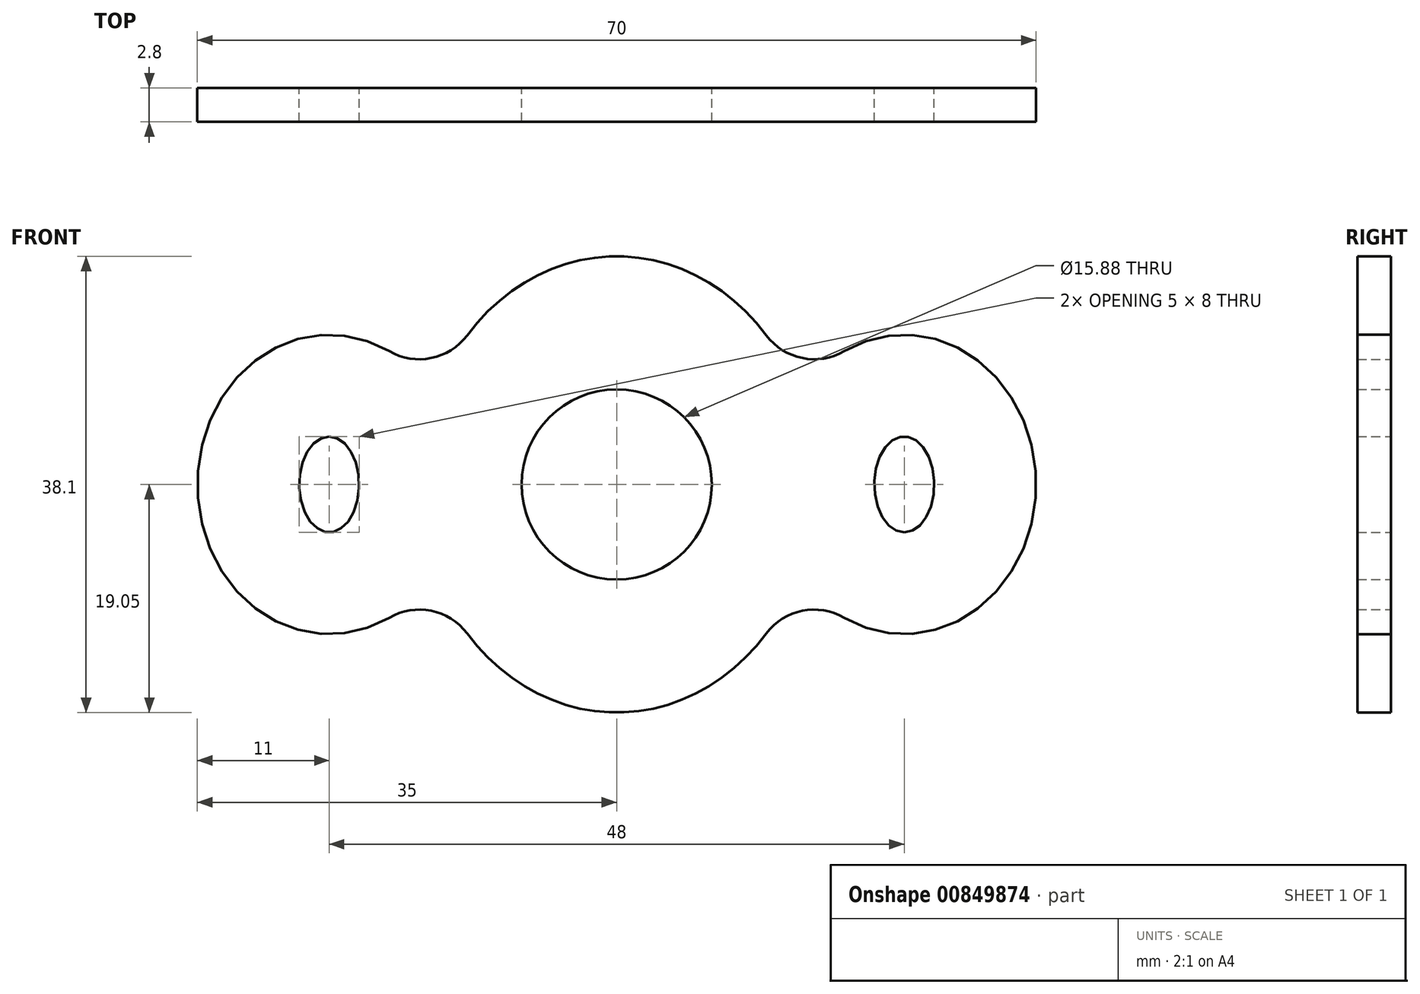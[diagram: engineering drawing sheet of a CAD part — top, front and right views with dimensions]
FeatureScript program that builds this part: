
annotation { "Feature Type Name" : "Feature", "Feature Type Description" : "" }
export const myFeature = defineFeature(function(context is Context, id is Id, definition is map)
    precondition{}
    {
        {
            var Q0;
            Q0=qCreatedBy(makeId("Front.planeOp"),FACE);
            var sketch = newSketch(context, id + "F0", { "sketchPlane" : qUnion([Q0])});
            skEllipse(sketch, "E0", {"center": v(0, 0) * mm, "majorRadius": 19.05 * mm, "minorRadius": 16.5 * mm, "majorAxis": v(0, 1)});
            skEllipse(sketch, "E1", {"center": v(0, 0) * mm, "majorRadius": 7.94 * mm, "minorRadius": 7.94 * mm, "majorAxis": v(0, 1)});
            skEllipse(sketch, "E2", {"center": v(24, 0) * mm, "majorRadius": 12.5 * mm, "minorRadius": 11 * mm, "majorAxis": v(0, 1)});
            skEllipse(sketch, "E3", {"center": v(-24, 0) * mm, "majorRadius": 12.5 * mm, "minorRadius": 11 * mm, "majorAxis": v(0, 1)});
            skEllipse(sketch, "E4", {"center": v(-24, 0) * mm, "majorRadius": 4 * mm, "minorRadius": 2.5 * mm, "majorAxis": v(0, 1)});
            skEllipse(sketch, "E5", {"center": v(24, 0) * mm, "majorRadius": 4 * mm, "minorRadius": 2.5 * mm, "majorAxis": v(0, -1)});
            skSolve(sketch);
        }
        {
            var Q0;
            Q0 = qSketchRegion(id + "F0", true);
            extrude(context, id + "F1", {"entities" : qUnion([Q0]), "depth" : 2.8 * mm, "offsetDistance" : 25 * mm});
        }
        {
            var Q0;
            {var subQ0=sQuery(id+"F0.wireOp",EDGE,"E2");var subQ1=sQuery(id+"F0.wireOp",EDGE,"E0");Q0=makeQuery(id+"F1.opExtrude","SWEPT_EDGE",EDGE,{"disambiguationData":[OSD([subQ1,subQ0]),TDD([makeQuery(id+"F0.imprint","INTERSECT",VERTEX,{"disambiguationData":[OD(0.0)],"derivedFrom":[subQ1,subQ0]})])]});}
            var Q1;
            {var subQ0=sQuery(id+"F0.wireOp",EDGE,"E3");var subQ1=sQuery(id+"F0.wireOp",EDGE,"E0");Q1=makeQuery(id+"F1.opExtrude","SWEPT_EDGE",EDGE,{"disambiguationData":[OSD([subQ1,subQ0]),TDD([makeQuery(id+"F0.imprint","INTERSECT",VERTEX,{"disambiguationData":[OD(0.0)],"derivedFrom":[subQ1,subQ0]})])]});}
            var Q2;
            {var subQ0=sQuery(id+"F0.wireOp",EDGE,"E3");var subQ1=sQuery(id+"F0.wireOp",EDGE,"E0");Q2=makeQuery(id+"F1.opExtrude","SWEPT_EDGE",EDGE,{"disambiguationData":[OSD([subQ1,subQ0]),TDD([makeQuery(id+"F0.imprint","INTERSECT",VERTEX,{"disambiguationData":[OD(1.0)],"derivedFrom":[subQ1,subQ0]})])]});}
            var Q3;
            {var subQ0=sQuery(id+"F0.wireOp",EDGE,"E2");var subQ1=sQuery(id+"F0.wireOp",EDGE,"E0");Q3=makeQuery(id+"F1.opExtrude","SWEPT_EDGE",EDGE,{"disambiguationData":[OSD([subQ1,subQ0]),TDD([makeQuery(id+"F0.imprint","INTERSECT",VERTEX,{"disambiguationData":[OD(1.0)],"derivedFrom":[subQ1,subQ0]})])]});}
            fillet(context, id + "F2", {"entities" : qUnion([Q0, Q1, Q2, Q3]), "radius" : 5 * mm, "tangentPropagation" : true, "allowEdgeOverflow" : false});
        }
    });
